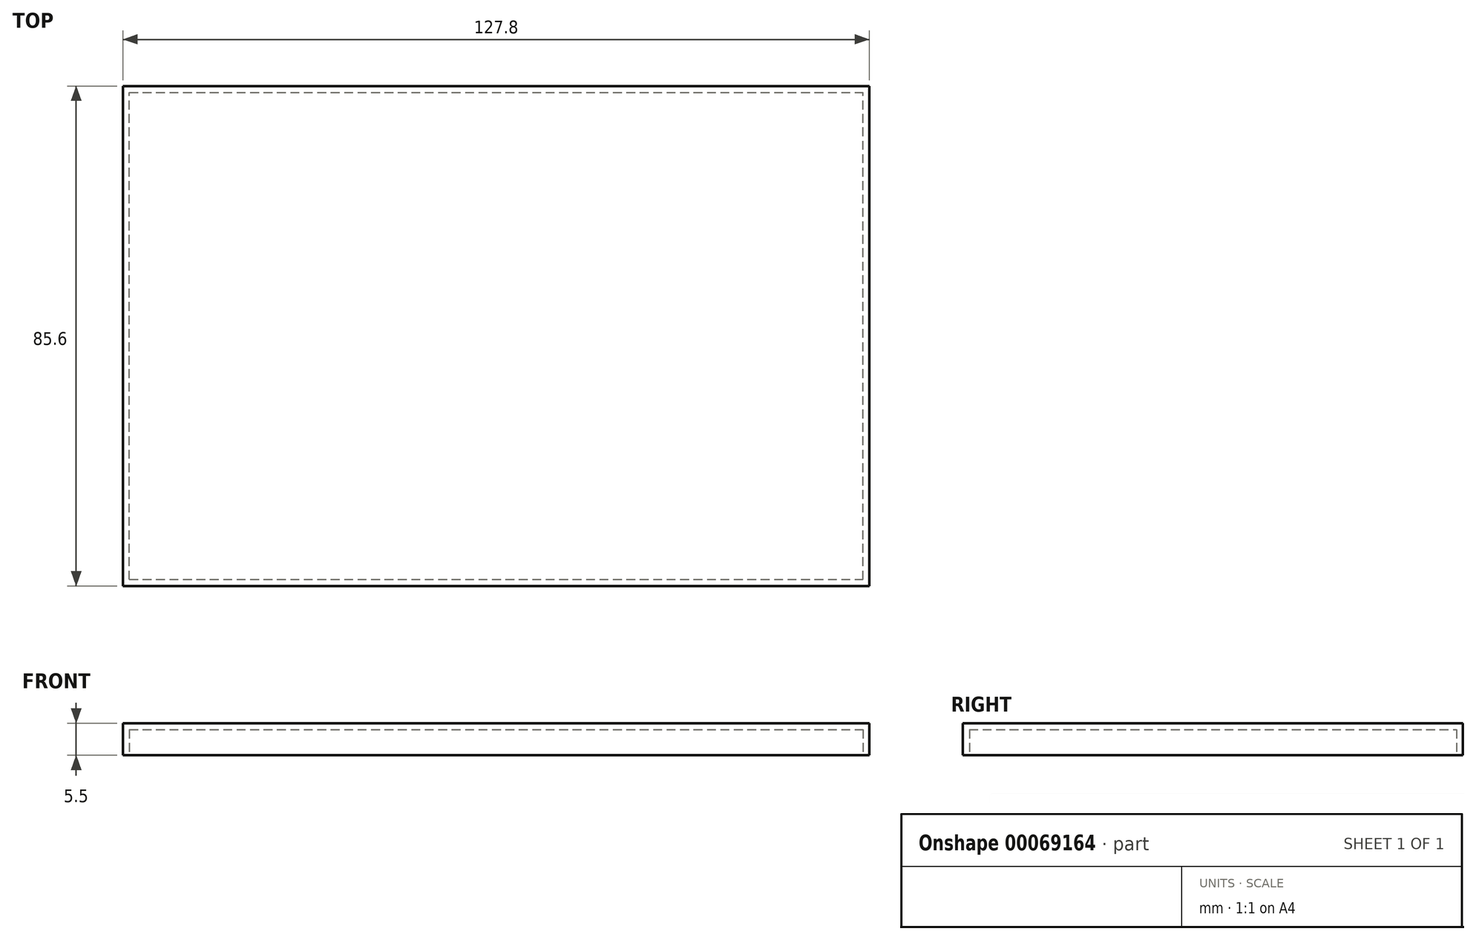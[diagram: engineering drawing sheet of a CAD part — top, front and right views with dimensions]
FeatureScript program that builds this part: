
annotation { "Feature Type Name" : "Feature", "Feature Type Description" : "" }
export const myFeature = defineFeature(function(context is Context, id is Id, definition is map)
    precondition{}
    {
        {
            var Q0;
            Q0=qCreatedBy(makeId("Top.planeOp"),FACE);
            var sketch = newSketch(context, id + "F0", { "sketchPlane" : qUnion([Q0])});
            skLineSegment(sketch, "E0.bottom", {"start": v(-63.9, -42.8) * mm, "end": v(63.9, -42.8) * mm});
            skLineSegment(sketch, "E0.top", {"start": v(-63.9, 42.8) * mm, "end": v(63.9, 42.8) * mm});
            skLineSegment(sketch, "E0.left", {"start": v(-63.9, -42.8) * mm, "end": v(-63.9, 42.8) * mm});
            skLineSegment(sketch, "E0.right", {"start": v(63.9, -42.8) * mm, "end": v(63.9, 42.8) * mm});
            skPoint(sketch, "E0.middle", {"position": v(0, 0) * mm});
            skSolve(sketch);
        }
        {
            var Q0;
            Q0 = qSketchRegion(id + "F0", true);
            extrude(context, id + "F1", {"entities" : qUnion([Q0]), "depth" : 5.5 * mm});
        }
        {
            var Q0;
            Q0=makeQuery(id+"F1.opExtrude","CAP_FACE",FACE,{"disambiguationData":[OSD([sQuery(id+"F0.wireOp",EDGE,"E0.bottom"),sQuery(id+"F0.wireOp",EDGE,"E0.top"),sQuery(id+"F0.wireOp",EDGE,"E0.left"),sQuery(id+"F0.wireOp",EDGE,"E0.right")])],"isStart":true});
            var sketch = newSketch(context, id + "F2", { "sketchPlane" : qUnion([Q0])});
            skLineSegment(sketch, "E1.0", {"start": v(-62.8, 41.7) * mm, "end": v(62.8, 41.7) * mm});
            skLineSegment(sketch, "E1.1", {"start": v(-62.8, 41.7) * mm, "end": v(-62.8, -41.7) * mm});
            skLineSegment(sketch, "E1.2", {"start": v(-62.8, -41.7) * mm, "end": v(62.8, -41.7) * mm});
            skLineSegment(sketch, "E1.3", {"start": v(62.8, 41.7) * mm, "end": v(62.8, -41.7) * mm});
            skSolve(sketch);
        }
        {
            var Q0;
            Q0 = qSketchRegion(id + "F2", true);
            var Q1;
            Q1=makeQuery(id+"F1.opExtrude","CAP_FACE",FACE,{"disambiguationData":[OSD([sQuery(id+"F0.wireOp",EDGE,"E0.bottom"),sQuery(id+"F0.wireOp",EDGE,"E0.top"),sQuery(id+"F0.wireOp",EDGE,"E0.left"),sQuery(id+"F0.wireOp",EDGE,"E0.right")])],"isStart":false});
            extrude(context, id + "F3", {"entities" : qUnion([Q0]), "operationType" : NewBodyOperationType.REMOVE, "oppositeDirection" : true, "endBoundEntityFace" : qUnion([Q1]), "depth" : 4.4 * mm});
        }
    });
